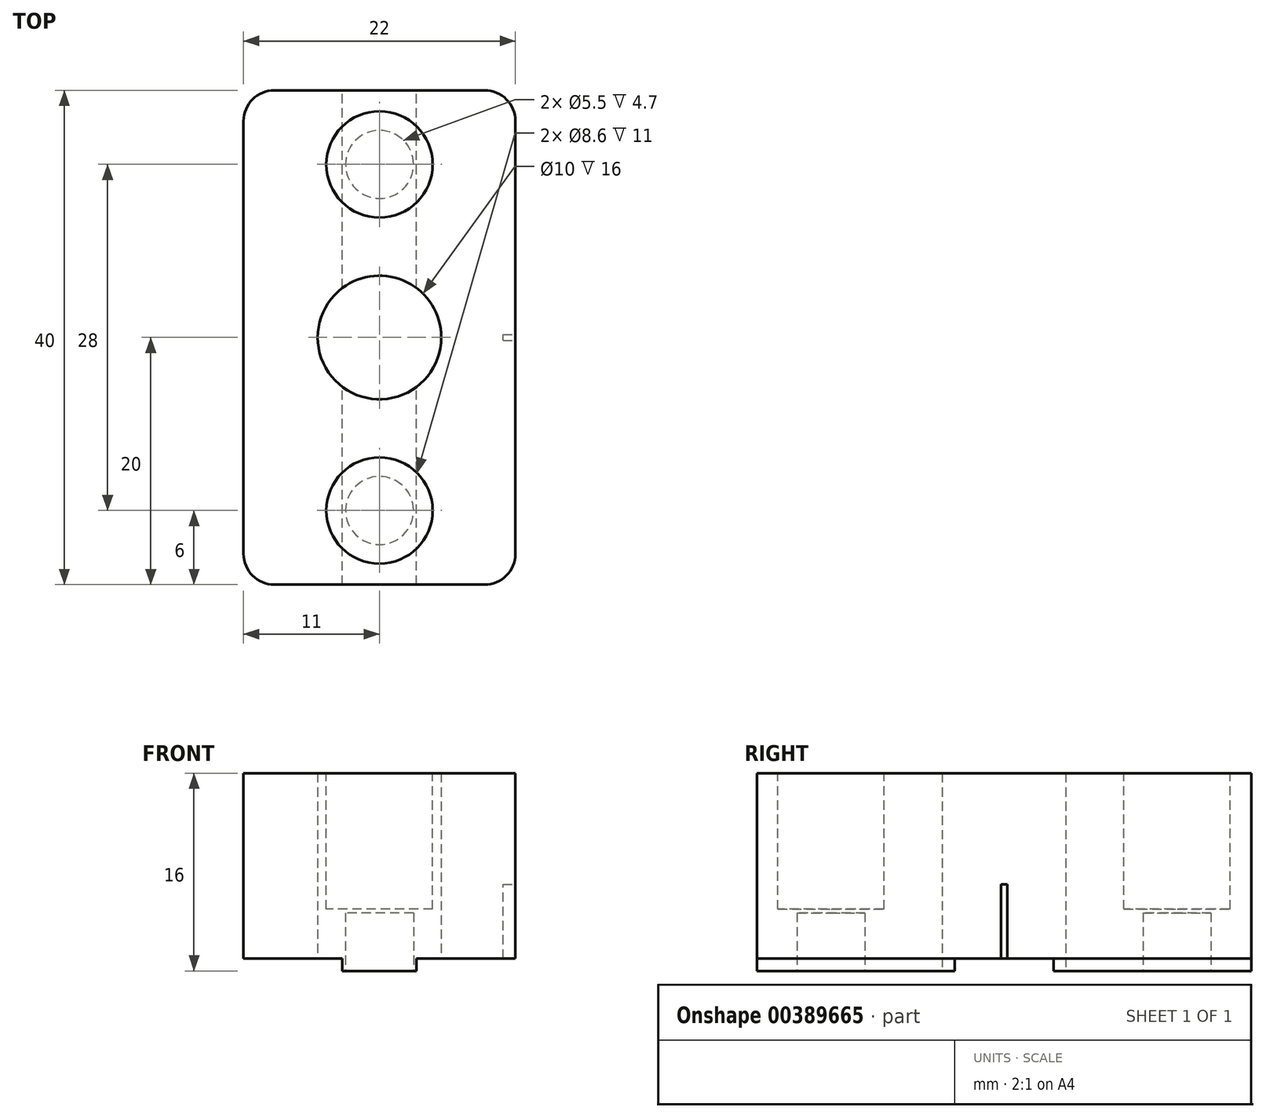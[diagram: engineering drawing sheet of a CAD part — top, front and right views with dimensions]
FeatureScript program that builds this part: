
annotation { "Feature Type Name" : "Feature", "Feature Type Description" : "" }
export const myFeature = defineFeature(function(context is Context, id is Id, definition is map)
    precondition{}
    {
        {
            var Q0;
            Q0=qCreatedBy(makeId("Top.planeOp"),FACE);
            var sketch = newSketch(context, id + "F0", { "sketchPlane" : qUnion([Q0])});
            skLineSegment(sketch, "E0.bottom", {"start": v(-11, 9) * mm, "end": v(11, 9) * mm});
            skLineSegment(sketch, "E0.top", {"start": v(-11, -9) * mm, "end": v(11, -9) * mm});
            skLineSegment(sketch, "E0.left", {"start": v(-11, 9) * mm, "end": v(-11, -9) * mm});
            skLineSegment(sketch, "E0.right", {"start": v(11, 9) * mm, "end": v(11, -9) * mm});
            skCircle(sketch, "E1", {"center": v(0, 0) * mm, "radius": 5 * mm});
            skLineSegment(sketch, "E2.bottom", {"start": v(-11, -20) * mm, "end": v(11, -20) * mm});
            skLineSegment(sketch, "E2.top", {"start": v(-11, 20) * mm, "end": v(11, 20) * mm});
            skLineSegment(sketch, "E2.left", {"start": v(-11, -20) * mm, "end": v(-11, 20) * mm});
            skLineSegment(sketch, "E2.right", {"start": v(11, -20) * mm, "end": v(11, 20) * mm});
            skCircle(sketch, "E3", {"center": v(0, 14) * mm, "radius": 2.75 * mm});
            skCircle(sketch, "E4", {"center": v(0, -14) * mm, "radius": 2.75 * mm});
            skSolve(sketch);
        }
        {
            var Q0;
            Q0=qCreatedBy(makeId("Top.planeOp"),FACE);
            var sketch = newSketch(context, id + "F1", { "sketchPlane" : qUnion([Q0])});
            skLineSegment(sketch, "E5.0", {"start": v(-11, -20) * mm, "end": v(-11, 20) * mm});
            skLineSegment(sketch, "E6.0", {"start": v(-11, -20) * mm, "end": v(11, -20) * mm});
            skLineSegment(sketch, "E7.0", {"start": v(11, -20) * mm, "end": v(11, 20) * mm});
            skLineSegment(sketch, "E8.0", {"start": v(-11, 20) * mm, "end": v(11, 20) * mm});
            skCircle(sketch, "E9.0", {"center": v(0, 14) * mm, "radius": 2.75 * mm});
            skCircle(sketch, "E10.0", {"center": v(0, -14) * mm, "radius": 2.75 * mm});
            skCircle(sketch, "E11.0", {"center": v(0, 0) * mm, "radius": 5 * mm});
            skSolve(sketch);
        }
        {
            var Q0;
            Q0=qSketchRegion(id+"F1",true);
            extrude(context, id + "F2", {"entities" : qUnion([Q0]), "depth" : 15 * mm});
        }
        {
            var Q0;
            Q0=makeQuery(id+"F2.opExtrude","CAP_FACE",FACE,{"disambiguationData":[OSD([sQuery(id+"F1.wireOp",EDGE,"E5.0"),sQuery(id+"F1.wireOp",EDGE,"E6.0"),sQuery(id+"F1.wireOp",EDGE,"E7.0"),sQuery(id+"F1.wireOp",EDGE,"E8.0"),sQuery(id+"F1.wireOp",EDGE,"E9.0"),sQuery(id+"F1.wireOp",EDGE,"E10.0"),sQuery(id+"F1.wireOp",EDGE,"E11.0")])],"isStart":false});
            var sketch = newSketch(context, id + "F3", { "sketchPlane" : qUnion([Q0])});
            skPoint(sketch, "E12", {"position": v(0, 14) * mm});
            skPoint(sketch, "E13", {"position": v(0, -14) * mm});
            skCircle(sketch, "E14", {"center": v(0, 14) * mm, "radius": 4.3 * mm});
            skCircle(sketch, "E15", {"center": v(0, -14) * mm, "radius": 4.3 * mm});
            skSolve(sketch);
        }
        {
            var Q0;
            Q0=qSketchRegion(id+"F3",true);
            extrude(context, id + "F4", {"entities" : qUnion([Q0]), "operationType" : NewBodyOperationType.REMOVE, "oppositeDirection" : true, "depth" : 11 * mm});
        }
        {
            var Q0;
            Q0=makeQuery(id+"F2.opExtrude","SWEPT_EDGE",EDGE,{"disambiguationData":[OSD([sQuery(id+"F1.wireOp",EDGE,"E6.0"),sQuery(id+"F1.wireOp",EDGE,"E7.0")])]});
            var Q1;
            Q1=makeQuery(id+"F2.opExtrude","SWEPT_EDGE",EDGE,{"disambiguationData":[OSD([sQuery(id+"F1.wireOp",EDGE,"E5.0"),sQuery(id+"F1.wireOp",EDGE,"E6.0")])]});
            var Q2;
            Q2=makeQuery(id+"F2.opExtrude","SWEPT_EDGE",EDGE,{"disambiguationData":[OSD([sQuery(id+"F1.wireOp",EDGE,"E7.0"),sQuery(id+"F1.wireOp",EDGE,"E8.0")])]});
            var Q3;
            Q3=makeQuery(id+"F2.opExtrude","SWEPT_EDGE",EDGE,{"disambiguationData":[OSD([sQuery(id+"F1.wireOp",EDGE,"E5.0"),sQuery(id+"F1.wireOp",EDGE,"E8.0")])]});
            fillet(context, id + "F5", {"entities" : qUnion([Q0, Q1, Q2, Q3]), "radius" : 2.5 * mm, "tangentPropagation" : true, "allowEdgeOverflow" : false});
        }
        {
            var Q0;
            {var subQ1=sQuery(id+"F0.wireOp",EDGE,"E0.top");Q0=makeQuery(id+"F0.imprint","IMPRINT",FACE,{"disambiguationData":[TD([[makeQuery(id+"F0.imprint","IMPRINT",EDGE,{"derivedFrom":subQ1}),-1.0]])]});}
            var sketch = newSketch(context, id + "F6", { "sketchPlane" : qUnion([Q0])});
            skPoint(sketch, "E16.0", {"position": v(0, -20) * mm});
            skPoint(sketch, "E17.0", {"position": v(0, 20) * mm});
            skLineSegment(sketch, "E18.bottom", {"start": v(0, -20) * mm, "end": v(3, -20) * mm});
            skLineSegment(sketch, "E18.top", {"start": v(0, 20) * mm, "end": v(3, 20) * mm});
            skLineSegment(sketch, "E18.right", {"start": v(3, -20) * mm, "end": v(3, -4) * mm});
            skLineSegment(sketch, "E19.MirrorCS", {"start": v(0, -20) * mm, "end": v(-3, -20) * mm});
            skLineSegment(sketch, "E20.MirrorCS", {"start": v(-3, -20) * mm, "end": v(-3, -4) * mm});
            skLineSegment(sketch, "E21.MirrorCS", {"start": v(0, 20) * mm, "end": v(-3, 20) * mm});
            skArc(sketch, "E22.0", {"start": v(-3, -4) * mm, "mid": v(0, -5) * mm, "end": v(3, -4) * mm});
            skCircle(sketch, "E22.1", {"center": v(0, 14) * mm, "radius": 2.75 * mm});
            skCircle(sketch, "E22.2", {"center": v(0, -14) * mm, "radius": 2.75 * mm});
            skLineSegment(sketch, "E23.trimOffspring", {"start": v(3, 4) * mm, "end": v(3, 20) * mm});
            skLineSegment(sketch, "E24.trimOffspring", {"start": v(-3, 4) * mm, "end": v(-3, 20) * mm});
            skArc(sketch, "E25.trimOffspring", {"start": v(3, 4) * mm, "mid": v(0, 5) * mm, "end": v(-3, 4) * mm});
            skSolve(sketch);
        }
        {
            var Q0;
            Q0=qSketchRegion(id+"F6",true);
            extrude(context, id + "F7", {"entities" : qUnion([Q0]), "operationType" : NewBodyOperationType.ADD, "oppositeDirection" : true, "depth" : 1 * mm});
        }
        {
            var Q0;
            Q0=makeQuery(id+"F4.boolean.opBoolean","COPY",FACE,{"derivedFrom":makeQuery(id+"F4.opExtrude","CAP_FACE",FACE,{"disambiguationData":[OSD([sQuery(id+"F3.wireOp",EDGE,"E14")])],"isStart":false})});
            var sketch = newSketch(context, id + "F8", { "sketchPlane" : qUnion([Q0])});
            skCircle(sketch, "E26.0", {"center": v(0, 14) * mm, "radius": 2.75 * mm});
            skCircle(sketch, "E27.0", {"center": v(0, -14) * mm, "radius": 2.75 * mm});
            skSolve(sketch);
        }
        {
            var Q0;
            Q0=qSketchRegion(id+"F8",true);
            extrude(context, id + "F9", {"entities" : qUnion([Q0]), "operationType" : NewBodyOperationType.ADD, "oppositeDirection" : true, "depth" : .3 * mm});
        }
        {
            var Q0;
            Q0=makeQuery(id+"F2.opExtrude","SWEPT_FACE",FACE,{"disambiguationData":[OSD([sQuery(id+"F1.wireOp",EDGE,"E7.0")])]});
            var sketch = newSketch(context, id + "F10", { "sketchPlane" : qUnion([Q0])});
            skLineSegment(sketch, "E28.bottom", {"start": v(0, 0) * mm, "end": v(0.25, 0) * mm});
            skLineSegment(sketch, "E28.top", {"start": v(0, 6) * mm, "end": v(0.25, 6) * mm});
            skLineSegment(sketch, "E28.left", {"start": v(0, 0) * mm, "end": v(0, 6) * mm});
            skLineSegment(sketch, "E28.right", {"start": v(0.25, 0) * mm, "end": v(0.25, 6) * mm});
            skLineSegment(sketch, "E29.MirrorCS", {"start": v(-0.25, 0) * mm, "end": v(-0.25, 6) * mm});
            skLineSegment(sketch, "E30.MirrorCS", {"start": v(0, 6) * mm, "end": v(-0.25, 6) * mm});
            skLineSegment(sketch, "E31.MirrorCS", {"start": v(0, 0) * mm, "end": v(-0.25, 0) * mm});
            skSolve(sketch);
        }
        {
            var Q0;
            Q0=qSketchRegion(id+"F10",true);
            extrude(context, id + "F11", {"entities" : qUnion([Q0]), "operationType" : NewBodyOperationType.REMOVE, "oppositeDirection" : true, "depth" : 1 * mm});
        }
    });
